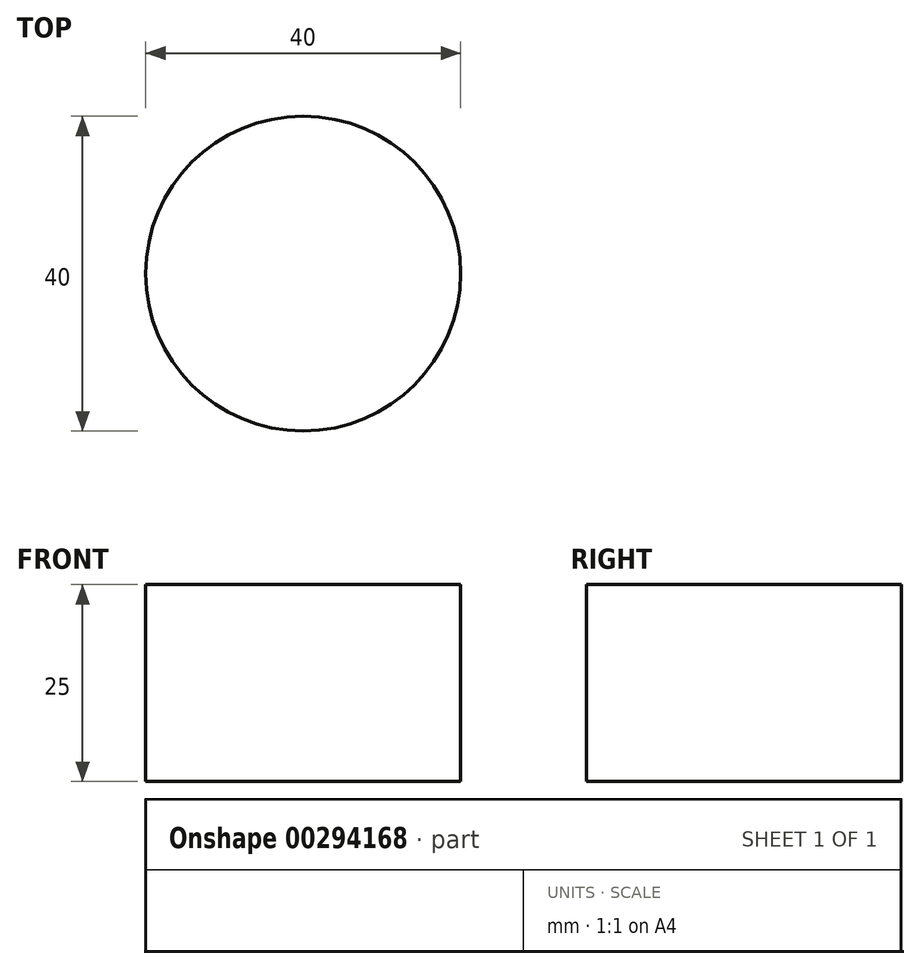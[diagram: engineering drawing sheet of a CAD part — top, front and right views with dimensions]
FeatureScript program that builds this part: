
annotation { "Feature Type Name" : "Feature", "Feature Type Description" : "" }
export const myFeature = defineFeature(function(context is Context, id is Id, definition is map)
    precondition{}
    {
        {
            var Q0;
            Q0=qCreatedBy(makeId("Top.planeOp"),FACE);
            var sketch = newSketch(context, id + "F0", { "sketchPlane" : qUnion([Q0])});
            skCircle(sketch, "E0", {"center": v(0, 0) * mm, "radius": 20 * mm});
            skSolve(sketch);
        }
        {
            var Q0;
            Q0 = qSketchRegion(id + "F0", true);
            extrude(context, id + "F1", {"entities" : qUnion([Q0]), "depth" : 25 * mm});
        }
    });
